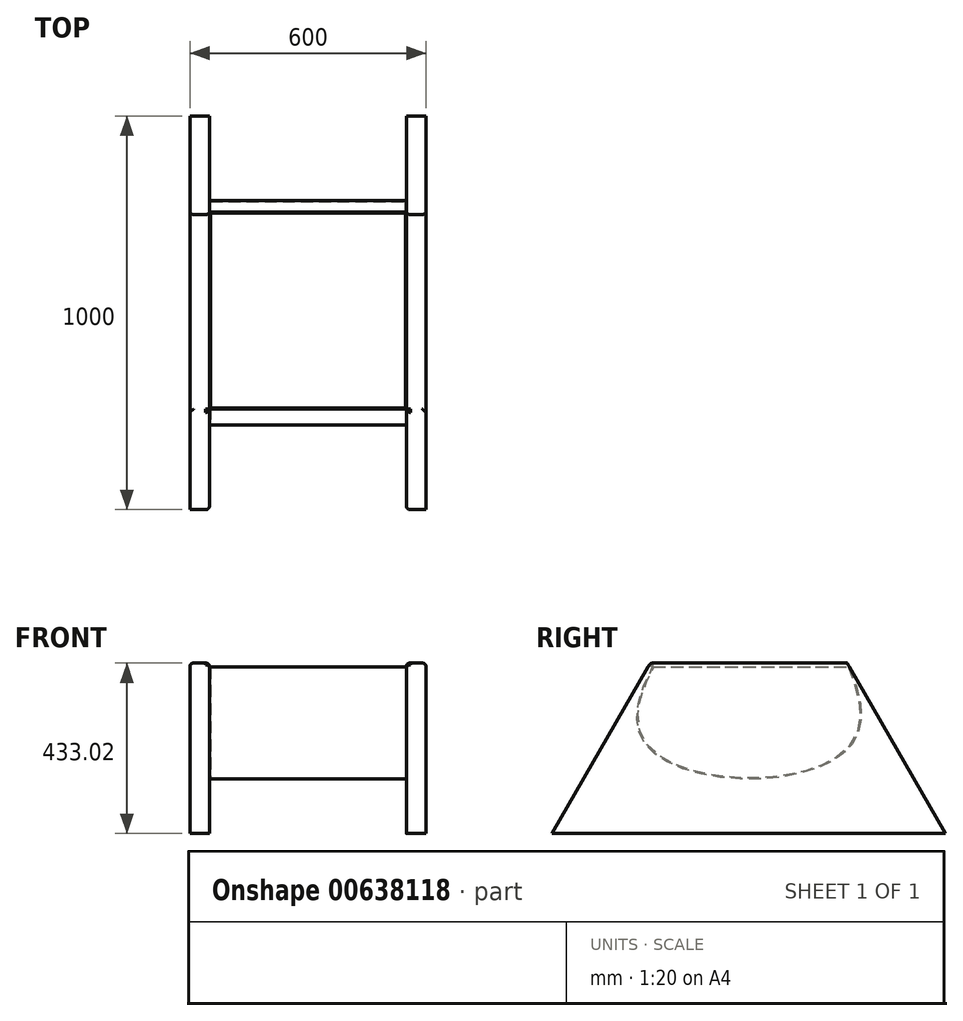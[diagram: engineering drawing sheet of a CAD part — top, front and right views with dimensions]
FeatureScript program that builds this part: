
annotation { "Feature Type Name" : "Feature", "Feature Type Description" : "" }
export const myFeature = defineFeature(function(context is Context, id is Id, definition is map)
    precondition{}
    {
        {
            var Q0;
            Q0=qCreatedBy(makeId("Right.planeOp"),FACE);
            var sketch = newSketch(context, id + "F0", { "sketchPlane" : qUnion([Q0])});
            skLineSegment(sketch, "E0", {"start": v(-500, -216.5) * mm, "end": v(500, -216.5) * mm});
            skLineSegment(sketch, "E1", {"start": v(500, -216.5) * mm, "end": v(250, 216.5) * mm});
            skLineSegment(sketch, "E2", {"start": v(250, 216.5) * mm, "end": v(-250, 216.5) * mm});
            skLineSegment(sketch, "E3", {"start": v(-250, 216.5) * mm, "end": v(-500, -216.5) * mm});
            skLineSegment(sketch, "E4", {"start": v(0, 492.56) * mm, "end": v(0, -513.4) * mm, "construction": true});
            skLineSegment(sketch, "E5", {"start": v(-656.25, 0) * mm, "end": v(724.7, 0) * mm, "construction": true});
            skSolve(sketch);
        }
        {
            var Q0;
            Q0 = qSketchRegion(id + "F0", true);
            extrude(context, id + "F1", {"entities" : qUnion([Q0]), "depth" : 50 * mm, "offsetDistance" : 25.4 * mm});
        }
        {
            var Q0;
            Q0=makeQuery(id+"F1.opExtrude","CAP_EDGE",EDGE,{"disambiguationData":[OSD([sQuery(id+"F0.wireOp",EDGE,"E2")])],"isStart":true});
            var Q1;
            Q1=makeQuery(id+"F1.opExtrude","CAP_EDGE",EDGE,{"disambiguationData":[OSD([sQuery(id+"F0.wireOp",EDGE,"E2")])],"isStart":false});
            var Q2;
            Q2=makeQuery(id+"F1.opExtrude","SWEPT_EDGE",EDGE,{"disambiguationData":[OSD([sQuery(id+"F0.wireOp",EDGE,"E2"),sQuery(id+"F0.wireOp",EDGE,"E3")])]});
            var Q3;
            Q3=makeQuery(id+"F1.opExtrude","CAP_EDGE",EDGE,{"disambiguationData":[OSD([sQuery(id+"F0.wireOp",EDGE,"E3")])],"isStart":true});
            fillet(context, id + "F2", {"entities" : qUnion([Q0, Q1, Q2, Q3]), "radius" : 10 * mm, "rho" : 0.5, "crossSection" : FilletCrossSection.CONIC, "allowEdgeOverflow" : false});
        }
        {
            var Q0;
            Q0=makeQuery(id+"F1.opExtrude","CAP_FACE",FACE,{"disambiguationData":[OSD([sQuery(id+"F0.wireOp",EDGE,"E0"),sQuery(id+"F0.wireOp",EDGE,"E1"),sQuery(id+"F0.wireOp",EDGE,"E2"),sQuery(id+"F0.wireOp",EDGE,"E3")])],"isStart":true});
            cPlane(context, id + "F3", {"entities" : qUnion([Q0]), "cplaneType" : CPlaneType.OFFSET, "offset" : 250 * mm, "width" : 152.4 * mm, "height" : 152.4 * mm});
        }
        {
            var Q0;
            Q0=makeQuery(id+"F1.opExtrude","SWEPT_BODY",BODY,{"disambiguationData":[OSD([sQuery(id+"F0.wireOp",EDGE,"E0"),sQuery(id+"F0.wireOp",EDGE,"E1"),sQuery(id+"F0.wireOp",EDGE,"E2"),sQuery(id+"F0.wireOp",EDGE,"E3")])]});
            var Q1;
            Q1=qCreatedBy(id+"F3.planeOp",FACE);
            mirror(context, id + "F4", {"entities" : qUnion([Q0]), "mirrorPlane" : qUnion([Q1])});
        }
        {
            var Q0;
            Q0=makeQuery(id+"F1.opExtrude","CAP_FACE",FACE,{"disambiguationData":[OSD([sQuery(id+"F0.wireOp",EDGE,"E0"),sQuery(id+"F0.wireOp",EDGE,"E1"),sQuery(id+"F0.wireOp",EDGE,"E2"),sQuery(id+"F0.wireOp",EDGE,"E3")])],"isStart":true});
            var sketch = newSketch(context, id + "F5", { "sketchPlane" : qUnion([Q0])});
            skPoint(sketch, "E6.2.internal.snap0", {"position": v(-5.77, -216.5) * mm});
            skFitSpline(sketch, "E6", {"points": [v(-255.77, 206.5) * mm, v(-255.77, 2.17) * mm, v(-5.77, -78.31) * mm, v(255.77, 2.17) * mm, v(244.23, 206.5) * mm], "startDerivative": vector(-492.26, -1190.76) * mm, "endDerivative": vector(-640.42, 1189.81) * mm});
            skLineSegment(sketch, "E7", {"start": v(-255.77, 206.5) * mm, "end": v(244.23, 206.5) * mm});
            skLineSegment(sketch, "E8", {"start": v(0, 176.02) * mm, "end": v(0, -187.34) * mm, "construction": true});
            skLineSegment(sketch, "E9", {"start": v(-172.32, 0) * mm, "end": v(191.05, 0) * mm, "construction": true});
            skSolve(sketch);
        }
        {
            var Q0;
            {var subQ0=sQuery(id+"F5.wireOp",EDGE,"E7");Q0=makeQuery(id+"F5.imprint","IMPRINT",FACE,{"disambiguationData":[TD([[makeQuery(id+"F5.imprint","IMPRINT",EDGE,{"derivedFrom":subQ0}),1.0]])]});}
            extrude(context, id + "F6", {"entities" : qUnion([Q0]), "endBound" : BoundingType.UP_TO_NEXT, "depth" : 25.4 * mm, "offsetDistance" : 25.4 * mm});
        }
        {
            var Q0;
            Q0=makeQuery(id+"F6.opExtrude","SWEPT_FACE",FACE,{"disambiguationData":[OSD([sQuery(id+"F5.wireOp",EDGE,"E7")])]});
            shell(context, id + "F7", {"entities" : qUnion([Q0]), "thickness" : 2.54 * mm});
        }
    });
